# Revit family: Haworth_BuzziBox
name_source: partatom
category: Furniture
revit_build: Autodesk Revit 2018 (Build: 20170223_1515(x64)
units: mm (PartAtom-declared; Revit-internal decimal feet)

## family parameters
Always vertical = Yes
Cut with Voids When Loaded = No
OmniClass Number = 23.40.70.14.64.21
OmniClass Title = Systems Furniture
Room Calculation Point = No
Shared = No
Work Plane-Based = No

## types (6) — shared parameters
Assembly Code = E2020200
Manufacturer = Haworth
Max. Depth = 19 177/256"
Max. Width = 27 143/256"
Min. Depth = 7 23/256"
Min. Width = 13 25/32"
Model = HCBZ-BXAB
Revision Number = 1
Size = Verify Final Dim. w/ Haworth
Standard Depths = 7.09, 9.84, 13.78, 15.75, 17.72, 19.69 in.
Standard Heights = 10.63, 13.78, 15.75, 17.72, 19.69 in.
Standard Widths = 13.78, 23.62, 25.59, 27.56 in.
URL = http://www.haworth.com
URL - Product = https://www.haworth.com
Warranty = http://www.haworth.com

## per-type parameters (varying)
| type | Actual Depth | Actual Height | Actual Width | Depth | Description | L Box | M Box | S Box | Width | XL Box | XS Box | XXS Box |
| HCBZ-BXAB-6 | 19 177/256" | 19 177/256" | 27 143/256" | 19 177/256" | Haworth BuzziBox XL Box | No | No | No | 27 143/256" | Yes | No | No |
| HCBZ-BXAB-5 | 17 23/32" | 17 23/32" | 25 151/256" | 17 23/32" | Haworth BuzziBox L Box | Yes | No | No | 25 151/256" | No | No | No |
| HCBZ-BXAB-4 | 15 3/4" | 15 3/4" | 23 159/256" | 15 3/4" | Haworth BuzziBox M Box | No | Yes | No | 23 159/256" | No | No | No |
| HCBZ-BXAB-3 | 13 25/32" | 13 25/32" | 13 25/32" | 13 25/32" | Haworth BuzziBox S Box | No | No | Yes | 13 25/32" | No | No | No |
| HCBZ-BXAB-2 | 9 215/256" | 10 161/256" | 13 25/32" | 9 215/256" | Haworth BuzziBox XS Box | No | No | No | 13 25/32" | No | Yes | No |
| HCBZ-BXAB-1 | 7 23/256" | 10 161/256" | 13 25/32" | 7 23/256" | Haworth BuzziBox XXS Box | No | No | No | 13 25/32" | No | No | Yes |

## geometry (parser evidence)
native form markers: Sweep x4
no freeform markers — native parametric forms only
